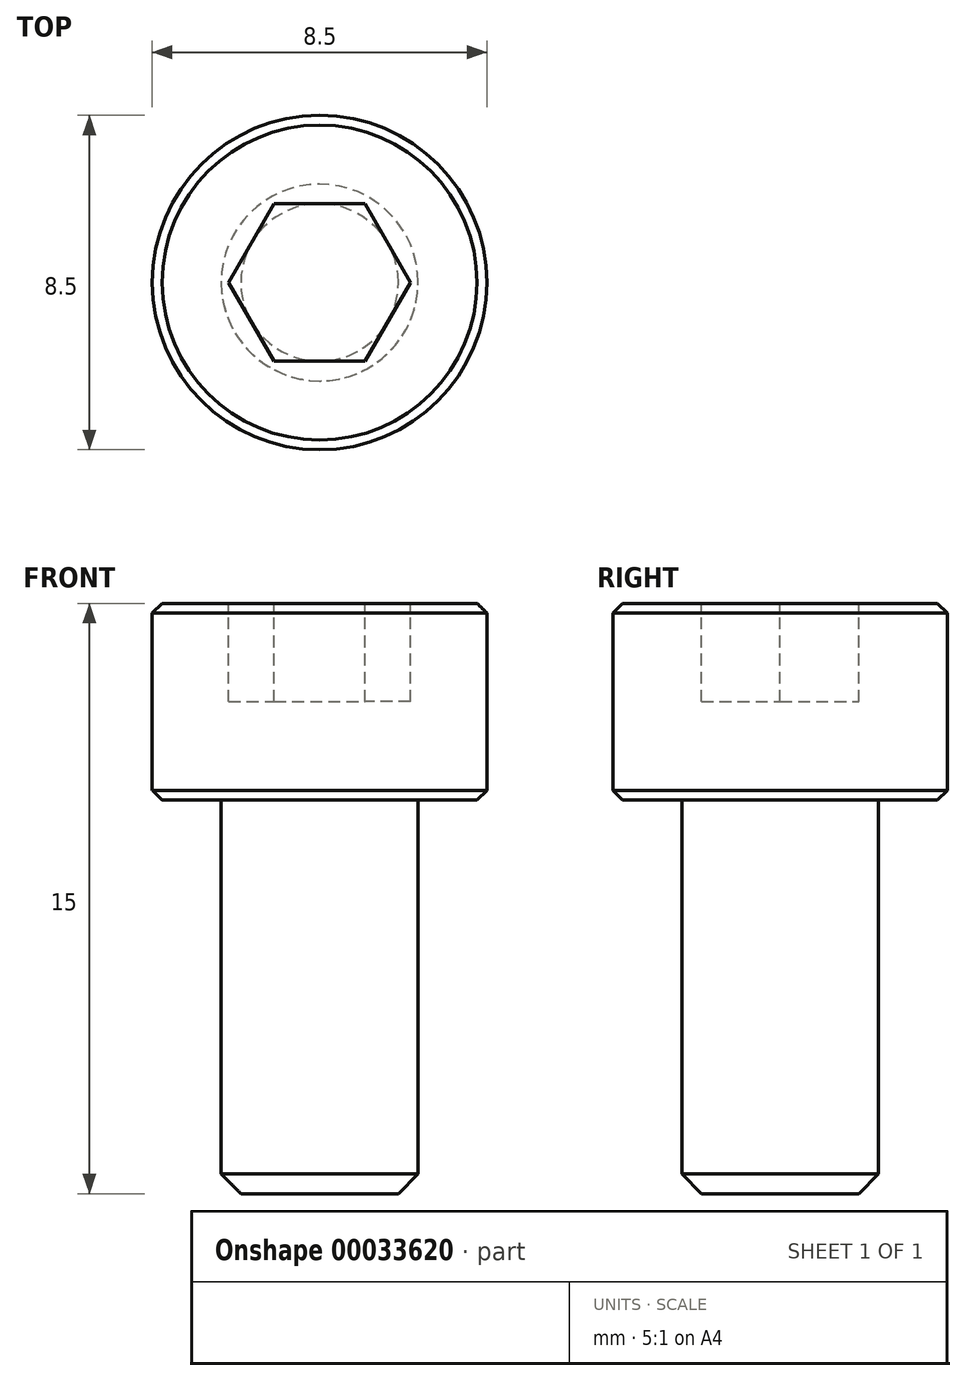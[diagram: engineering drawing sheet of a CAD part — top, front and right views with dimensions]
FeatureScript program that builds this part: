
annotation { "Feature Type Name" : "Feature", "Feature Type Description" : "" }
export const myFeature = defineFeature(function(context is Context, id is Id, definition is map)
    precondition{}
    {
        {
            var Q0;
            Q0=qCreatedBy(makeId("Front.planeOp"),FACE);
            var sketch = newSketch(context, id + "F0", { "sketchPlane" : qUnion([Q0])});
            skLineSegment(sketch, "E0", {"start": v(0, 0) * mm, "end": v(4.25, 0) * mm});
            skLineSegment(sketch, "E1", {"start": v(4.25, 0) * mm, "end": v(4.25, -5) * mm});
            skLineSegment(sketch, "E2", {"start": v(4.25, -5) * mm, "end": v(2.5, -5) * mm});
            skLineSegment(sketch, "E3", {"start": v(2.5, -5) * mm, "end": v(2.5, -15) * mm});
            skLineSegment(sketch, "E4", {"start": v(2.5, -15) * mm, "end": v(0, -15) * mm});
            skLineSegment(sketch, "E5", {"start": v(0, 0) * mm, "end": v(0, -15) * mm});
            skLineSegment(sketch, "E6", {"start": v(0, 0) * mm, "end": v(0, 2.24) * mm, "construction": true});
            skSolve(sketch);
        }
        {
            var Q0;
            Q0 = qSketchRegion(id + "F0", true);
            var Q1;
            Q1=sQuery(id+"F0.wireOp",EDGE,"E5");
            revolve(context, id + "F1", {"entities" : qUnion([Q0]), "axis" : qUnion([Q1]), "revolveType" : RevolveType.FULL});
        }
        {
            var Q0;
            Q0=makeQuery(id+"F1.opRevolve","SWEPT_FACE",FACE,{"disambiguationData":[OSD([sQuery(id+"F0.wireOp",EDGE,"E0")])]});
            var sketch = newSketch(context, id + "F2", { "sketchPlane" : qUnion([Q0])});
            skCircle(sketch, "E7.cCircle", {"center": v(0, 0) * mm, "radius": 2 * mm, "construction": true});
            skLineSegment(sketch, "E7.0", {"start": v(-1.15, 2) * mm, "end": v(1.15, 2) * mm});
            skLineSegment(sketch, "E7.1", {"start": v(1.15, 2) * mm, "end": v(2.3, 0) * mm});
            skLineSegment(sketch, "E7.2", {"start": v(2.3, 0) * mm, "end": v(1.15, -2) * mm});
            skLineSegment(sketch, "E7.3", {"start": v(1.15, -2) * mm, "end": v(-1.15, -2) * mm});
            skLineSegment(sketch, "E7.4", {"start": v(-1.15, -2) * mm, "end": v(-2.3, 0) * mm});
            skLineSegment(sketch, "E7.5", {"start": v(-2.3, 0) * mm, "end": v(-1.15, 2) * mm});
            skPoint(sketch, "E7.0.midPoint", {"position": v(0, 2) * mm});
            skSolve(sketch);
        }
        {
            var Q0;
            Q0 = qSketchRegion(id + "F2", true);
            extrude(context, id + "F3", {"entities" : qUnion([Q0]), "operationType" : NewBodyOperationType.REMOVE, "oppositeDirection" : true, "depth" : 2.5 * mm});
        }
        {
            var Q0;
            Q0=makeQuery(id+"F1.opRevolve","SWEPT_EDGE",EDGE,{"disambiguationData":[OSD([sQuery(id+"F0.wireOp",EDGE,"E3"),sQuery(id+"F0.wireOp",EDGE,"E4")])]});
            chamfer(context, id + "F4", {"entities" : qUnion([Q0]), "width" : 0.5 * mm, "tangentPropagation" : true});
        }
        {
            var Q0;
            Q0=makeQuery(id+"F1.opRevolve","SWEPT_EDGE",EDGE,{"disambiguationData":[OSD([sQuery(id+"F0.wireOp",EDGE,"E0"),sQuery(id+"F0.wireOp",EDGE,"E1")])]});
            var Q1;
            Q1=makeQuery(id+"F1.opRevolve","SWEPT_EDGE",EDGE,{"disambiguationData":[OSD([sQuery(id+"F0.wireOp",EDGE,"E1"),sQuery(id+"F0.wireOp",EDGE,"E2")])]});
            chamfer(context, id + "F5", {"entities" : qUnion([Q0, Q1]), "width" : 0.25 * mm, "tangentPropagation" : true});
        }
    });
